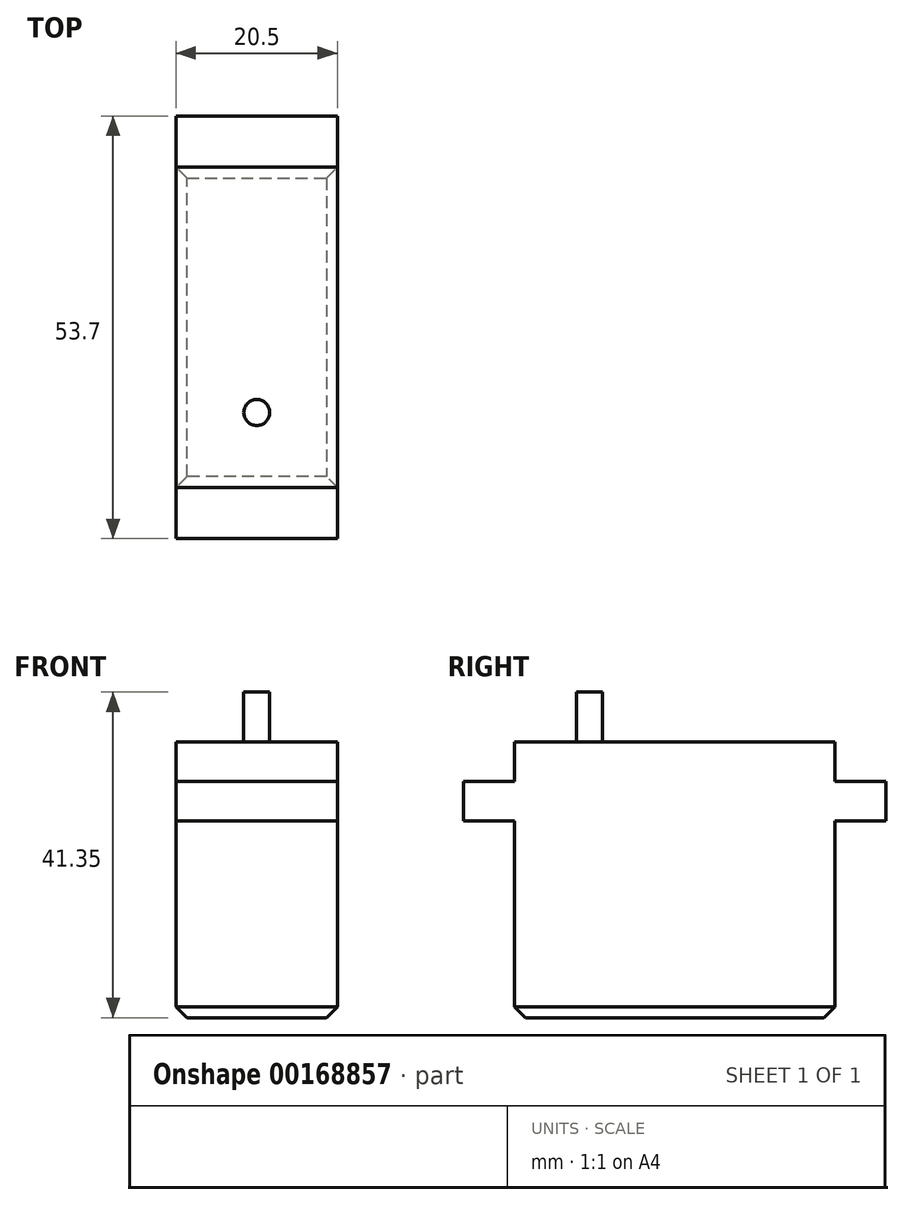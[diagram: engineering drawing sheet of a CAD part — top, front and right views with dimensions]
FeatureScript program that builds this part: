
annotation { "Feature Type Name" : "Feature", "Feature Type Description" : "" }
export const myFeature = defineFeature(function(context is Context, id is Id, definition is map)
    precondition{}
    {
        {
            var Q0;
            Q0=qCreatedBy(makeId("Top.planeOp"),FACE);
            var sketch = newSketch(context, id + "F0", { "sketchPlane" : qUnion([Q0])});
            skLineSegment(sketch, "E0.bottom", {"start": v(10.25, -20.35) * mm, "end": v(-10.25, -20.35) * mm});
            skLineSegment(sketch, "E0.top", {"start": v(10.25, 20.35) * mm, "end": v(-10.25, 20.35) * mm});
            skLineSegment(sketch, "E0.left", {"start": v(10.25, -20.35) * mm, "end": v(10.25, 20.35) * mm});
            skLineSegment(sketch, "E0.right", {"start": v(-10.25, -20.35) * mm, "end": v(-10.25, 20.35) * mm});
            skPoint(sketch, "E0.middle", {"position": v(0, 0) * mm});
            skSolve(sketch);
        }
        {
            var Q0;
            Q0 = qSketchRegion(id + "F0", true);
            extrude(context, id + "F1", {"entities" : qUnion([Q0]), "depth" : 35 * mm});
        }
        {
            var Q0;
            Q0=makeQuery(id+"F1.opExtrude","CAP_FACE",FACE,{"disambiguationData":[OSD([sQuery(id+"F0.wireOp",EDGE,"E0.bottom"),sQuery(id+"F0.wireOp",EDGE,"E0.top"),sQuery(id+"F0.wireOp",EDGE,"E0.left"),sQuery(id+"F0.wireOp",EDGE,"E0.right")])],"isStart":false});
            var sketch = newSketch(context, id + "F2", { "sketchPlane" : qUnion([Q0])});
            skCircle(sketch, "E1", {"center": v(0, -10.82) * mm, "radius": 1.65 * mm});
            skSolve(sketch);
        }
        {
            var Q0;
            Q0 = qSketchRegion(id + "F2", true);
            extrude(context, id + "F3", {"entities" : qUnion([Q0]), "operationType" : NewBodyOperationType.ADD, "depth" : 6.35 * mm});
        }
        {
            var Q0;
            Q0=makeQuery(id+"F1.opExtrude","SWEPT_FACE",FACE,{"disambiguationData":[OSD([sQuery(id+"F0.wireOp",EDGE,"E0.bottom")])]});
            var sketch = newSketch(context, id + "F4", { "sketchPlane" : qUnion([Q0])});
            skLineSegment(sketch, "E2.bottom", {"start": v(-10.25, 30) * mm, "end": v(10.25, 30) * mm});
            skLineSegment(sketch, "E2.top", {"start": v(-10.25, 25) * mm, "end": v(10.25, 25) * mm});
            skLineSegment(sketch, "E2.left", {"start": v(-10.25, 30) * mm, "end": v(-10.25, 25) * mm});
            skLineSegment(sketch, "E2.right", {"start": v(10.25, 30) * mm, "end": v(10.25, 25) * mm});
            skSolve(sketch);
        }
        {
            var Q0;
            Q0 = qSketchRegion(id + "F4", true);
            extrude(context, id + "F5", {"entities" : qUnion([Q0]), "operationType" : NewBodyOperationType.ADD, "depth" : 6.5 * mm});
        }
        {
            var Q0;
            Q0=makeQuery(id+"F1.opExtrude","SWEPT_FACE",FACE,{"disambiguationData":[OSD([sQuery(id+"F0.wireOp",EDGE,"E0.top")])]});
            var sketch = newSketch(context, id + "F6", { "sketchPlane" : qUnion([Q0])});
            skLineSegment(sketch, "E3.bottom", {"start": v(10.25, 25) * mm, "end": v(-10.25, 25) * mm});
            skLineSegment(sketch, "E3.top", {"start": v(10.25, 30) * mm, "end": v(-10.25, 30) * mm});
            skLineSegment(sketch, "E3.left", {"start": v(10.25, 25) * mm, "end": v(10.25, 30) * mm});
            skLineSegment(sketch, "E3.right", {"start": v(-10.25, 25) * mm, "end": v(-10.25, 30) * mm});
            skSolve(sketch);
        }
        {
            var Q0;
            Q0 = qSketchRegion(id + "F6", true);
            extrude(context, id + "F7", {"entities" : qUnion([Q0]), "operationType" : NewBodyOperationType.ADD, "depth" : 6.5 * mm});
        }
        {
            var Q0;
            Q0=makeQuery(id+"F1.opExtrude","CAP_EDGE",EDGE,{"disambiguationData":[OSD([sQuery(id+"F0.wireOp",EDGE,"E0.bottom")])],"isStart":true});
            var Q1;
            Q1=makeQuery(id+"F1.opExtrude","CAP_EDGE",EDGE,{"disambiguationData":[OSD([sQuery(id+"F0.wireOp",EDGE,"E0.left")])],"isStart":true});
            var Q2;
            Q2=makeQuery(id+"F1.opExtrude","CAP_EDGE",EDGE,{"disambiguationData":[OSD([sQuery(id+"F0.wireOp",EDGE,"E0.right")])],"isStart":true});
            var Q3;
            Q3=makeQuery(id+"F1.opExtrude","CAP_EDGE",EDGE,{"disambiguationData":[OSD([sQuery(id+"F0.wireOp",EDGE,"E0.top")])],"isStart":true});
            chamfer(context, id + "F8", {"entities" : qUnion([Q0, Q1, Q2, Q3]), "width" : 1.4 * mm, "tangentPropagation" : true});
        }
    });
